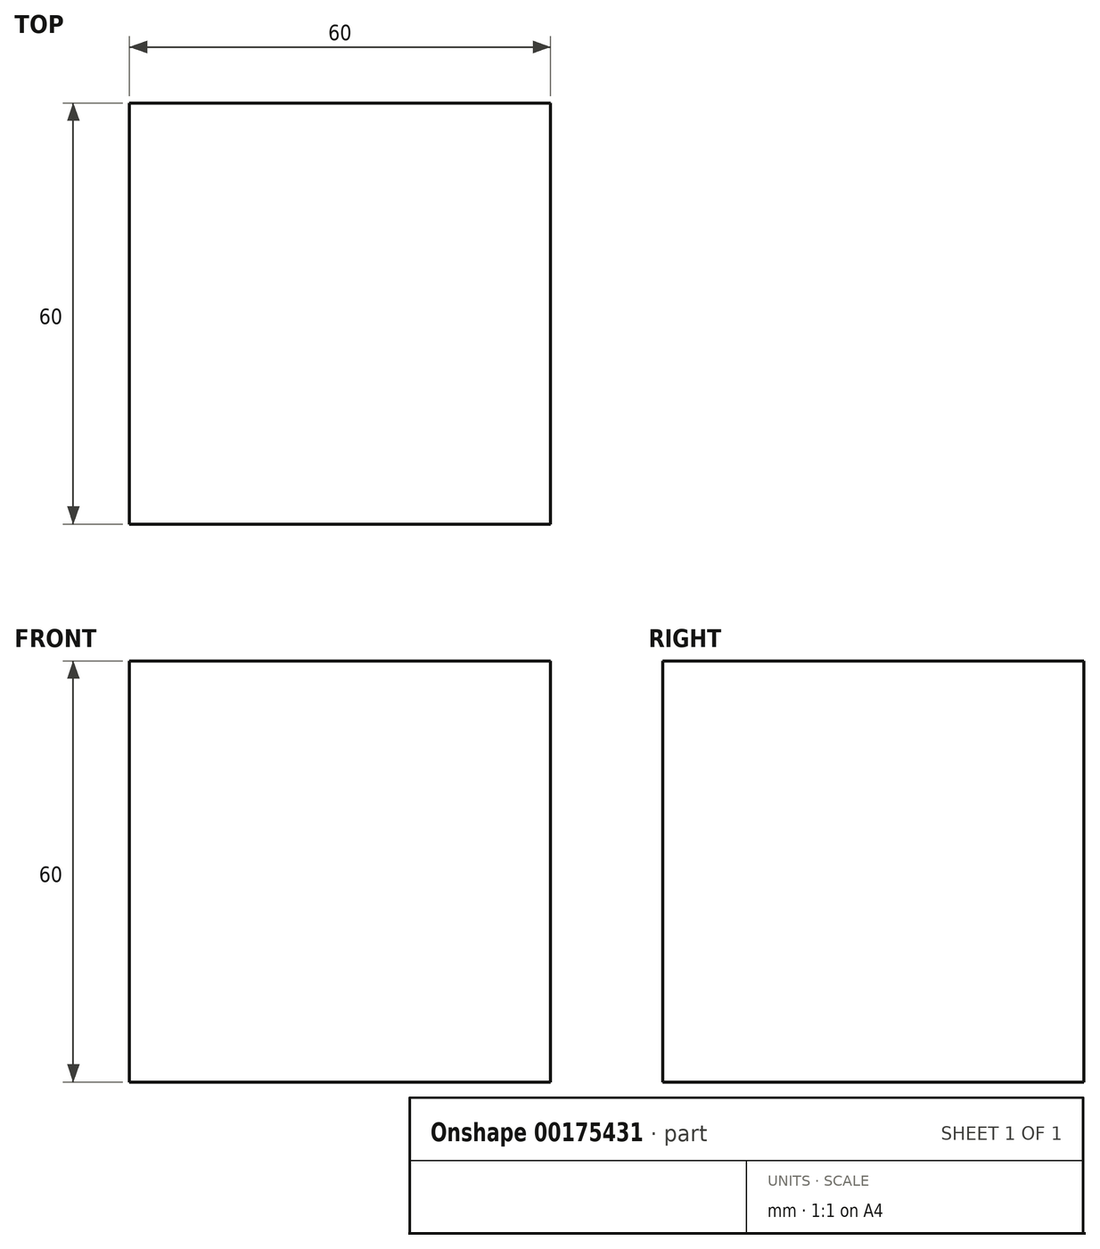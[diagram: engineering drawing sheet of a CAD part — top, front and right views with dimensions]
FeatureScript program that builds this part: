
annotation { "Feature Type Name" : "Feature", "Feature Type Description" : "" }
export const myFeature = defineFeature(function(context is Context, id is Id, definition is map)
    precondition{}
    {
        {
            var Q0;
            Q0=qCreatedBy(makeId("Top.planeOp"),FACE);
            var sketch = newSketch(context, id + "F0", { "sketchPlane" : qUnion([Q0])});
            skLineSegment(sketch, "E0.bottom", {"start": v(-23.93, 18.48) * mm, "end": v(36.07, 18.48) * mm});
            skLineSegment(sketch, "E0.top", {"start": v(-23.93, -41.52) * mm, "end": v(36.07, -41.52) * mm});
            skLineSegment(sketch, "E0.left", {"start": v(-23.93, 18.48) * mm, "end": v(-23.93, -41.52) * mm});
            skLineSegment(sketch, "E0.right", {"start": v(36.07, 18.48) * mm, "end": v(36.07, -41.52) * mm});
            skSolve(sketch);
        }
        {
            var Q0;
            Q0=makeQuery(id+"F0.imprint","IMPRINT",FACE,{"disambiguationData":[TD([[makeQuery(id+"F0.imprint","IMPRINT",EDGE,{"derivedFrom":sQuery(id+"F0.wireOp",EDGE,"E0.bottom")}),-1.0]])]});
            extrude(context, id + "F1", {"entities" : qUnion([Q0]), "depth" : 60 * mm});
        }
    });
